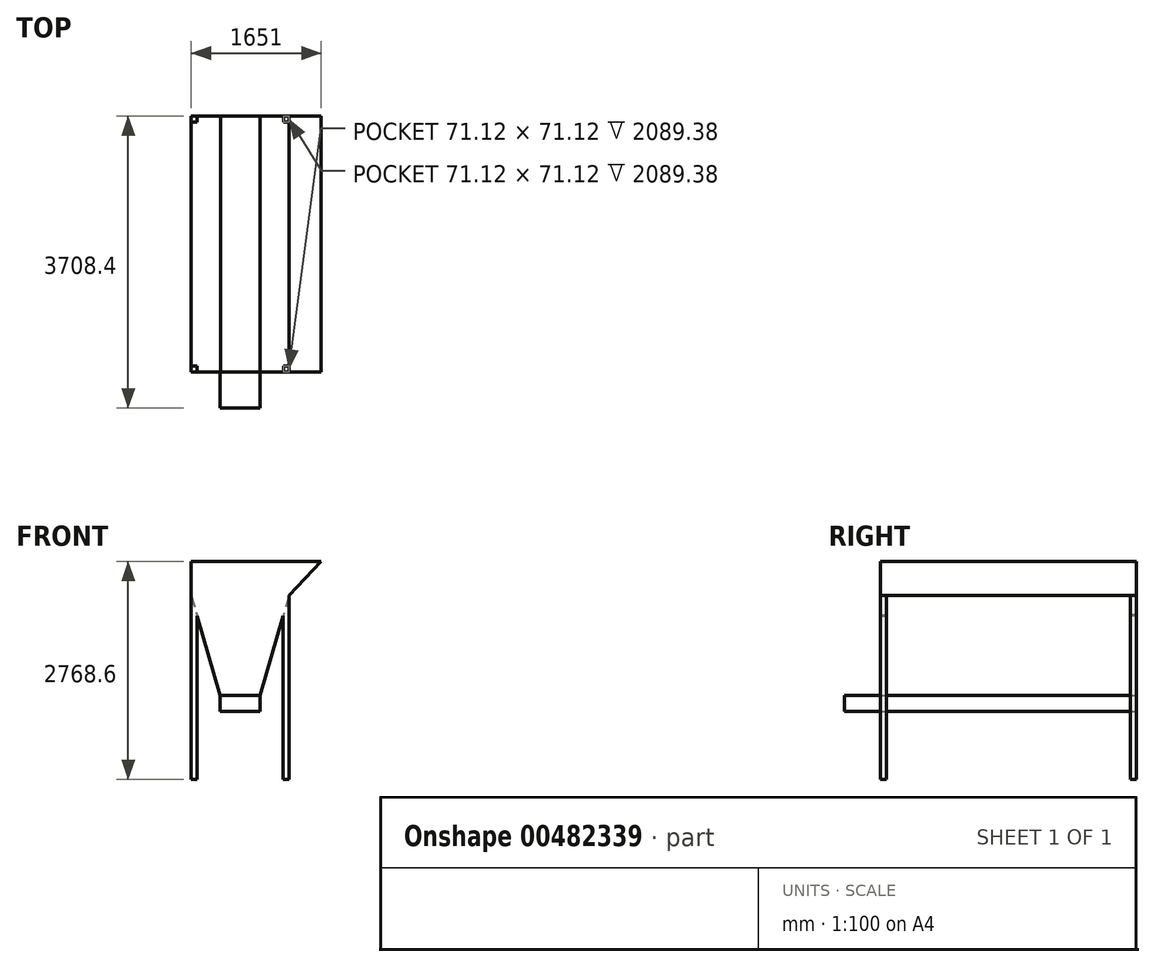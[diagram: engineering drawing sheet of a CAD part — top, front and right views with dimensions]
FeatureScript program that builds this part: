
annotation { "Feature Type Name" : "Feature", "Feature Type Description" : "" }
export const myFeature = defineFeature(function(context is Context, id is Id, definition is map)
    precondition{}
    {
        {
            var Q0;
            Q0=qCreatedBy(makeId("Front.planeOp"),FACE);
            var sketch = newSketch(context, id + "F0", { "sketchPlane" : qUnion([Q0])});
            skLineSegment(sketch, "E0", {"start": v(0, 0) * mm, "end": v(508, 0) * mm});
            skLineSegment(sketch, "E1", {"start": v(508, 0) * mm, "end": v(508, 203.2) * mm});
            skLineSegment(sketch, "E2", {"start": v(508, 203.2) * mm, "end": v(0, 203.2) * mm});
            skLineSegment(sketch, "E3", {"start": v(0, 203.2) * mm, "end": v(0, 0) * mm});
            skLineSegment(sketch, "E4", {"start": v(0, 203.2) * mm, "end": v(-368.3, 1473.2) * mm});
            skLineSegment(sketch, "E5", {"start": v(-368.3, 1473.2) * mm, "end": v(876.3, 1473.2) * mm});
            skLineSegment(sketch, "E6", {"start": v(876.3, 1473.2) * mm, "end": v(508, 203.2) * mm});
            skLineSegment(sketch, "E7", {"start": v(876.3, 1473.2) * mm, "end": v(1282.7, 1905) * mm});
            skLineSegment(sketch, "E8", {"start": v(1282.7, 1905) * mm, "end": v(-368.3, 1905) * mm});
            skLineSegment(sketch, "E9", {"start": v(-368.3, 1905) * mm, "end": v(-368.3, 1473.2) * mm});
            skSolve(sketch);
        }
        {
            var Q0;
            Q0 = qSketchRegion(id + "F0", true);
            extrude(context, id + "F1", {"entities" : qUnion([Q0]), "depth" : 3251.2 * mm, "offsetDistance" : 25.4 * mm});
        }
        {
            var Q0;
            Q0=makeQuery(id+"F1.opExtrude","SWEPT_FACE",FACE,{"disambiguationData":[OSD([sQuery(id+"F0.wireOp",EDGE,"E0")])]});
            cPlane(context, id + "F2", {"entities" : qUnion([Q0]), "cplaneType" : CPlaneType.OFFSET, "offset" : 863.6 * mm, "width" : 152.4 * mm, "height" : 152.4 * mm});
        }
        {
            var Q0;
            Q0=qCreatedBy(id+"F2.planeOp",FACE);
            var sketch = newSketch(context, id + "F3", { "sketchPlane" : qUnion([Q0])});
            skLineSegment(sketch, "E10.bottom", {"start": v(-292.1, 3175) * mm, "end": v(-368.3, 3175) * mm});
            skLineSegment(sketch, "E10.top", {"start": v(-292.1, 3251.2) * mm, "end": v(-368.3, 3251.2) * mm});
            skLineSegment(sketch, "E10.left", {"start": v(-292.1, 3175) * mm, "end": v(-292.1, 3251.2) * mm});
            skLineSegment(sketch, "E10.right", {"start": v(-368.3, 3175) * mm, "end": v(-368.3, 3251.2) * mm});
            skLineSegment(sketch, "E11.bottom", {"start": v(800.1, 3175) * mm, "end": v(876.3, 3175) * mm});
            skLineSegment(sketch, "E11.top", {"start": v(800.1, 3251.2) * mm, "end": v(876.3, 3251.2) * mm});
            skLineSegment(sketch, "E11.left", {"start": v(800.1, 3175) * mm, "end": v(800.1, 3251.2) * mm});
            skLineSegment(sketch, "E11.right", {"start": v(876.3, 3175) * mm, "end": v(876.3, 3251.2) * mm});
            skLineSegment(sketch, "E12.bottom", {"start": v(-292.1, 76.2) * mm, "end": v(-368.3, 76.2) * mm});
            skLineSegment(sketch, "E12.top", {"start": v(-292.1, 0) * mm, "end": v(-368.3, 0) * mm});
            skLineSegment(sketch, "E12.left", {"start": v(-292.1, 76.2) * mm, "end": v(-292.1, 0) * mm});
            skLineSegment(sketch, "E12.right", {"start": v(-368.3, 76.2) * mm, "end": v(-368.3, 0) * mm});
            skLineSegment(sketch, "E13.bottom", {"start": v(800.1, 76.2) * mm, "end": v(876.3, 76.2) * mm});
            skLineSegment(sketch, "E13.top", {"start": v(800.1, 0) * mm, "end": v(876.3, 0) * mm});
            skLineSegment(sketch, "E13.left", {"start": v(800.1, 76.2) * mm, "end": v(800.1, 0) * mm});
            skLineSegment(sketch, "E13.right", {"start": v(876.3, 76.2) * mm, "end": v(876.3, 0) * mm});
            skSolve(sketch);
        }
        {
            var Q0;
            Q0 = qSketchRegion(id + "F3", true);
            extrude(context, id + "F4", {"entities" : qUnion([Q0]), "operationType" : NewBodyOperationType.ADD, "endBound" : BoundingType.UP_TO_NEXT, "oppositeDirection" : true, "depth" : 25.4 * mm, "offsetDistance" : 25.4 * mm});
        }
        {
            var Q0;
            Q0=makeQuery(id+"F4.boolean.opBoolean","MERGE",FACE,{"derivedFrom":[makeQuery(id+"F1.opExtrude","CAP_FACE",FACE,{"disambiguationData":[OSD([sQuery(id+"F0.wireOp",EDGE,"E0"),sQuery(id+"F0.wireOp",EDGE,"E1"),sQuery(id+"F0.wireOp",EDGE,"E3"),sQuery(id+"F0.wireOp",EDGE,"E4"),sQuery(id+"F0.wireOp",EDGE,"E6"),sQuery(id+"F0.wireOp",EDGE,"E7"),sQuery(id+"F0.wireOp",EDGE,"E8"),sQuery(id+"F0.wireOp",EDGE,"E9")])],"isStart":false}),makeQuery(id+"F4.opExtrude","SWEPT_FACE",FACE,{"disambiguationData":[OSD([sQuery(id+"F3.wireOp",EDGE,"E10.top")])]}),makeQuery(id+"F4.opExtrude","SWEPT_FACE",FACE,{"disambiguationData":[OSD([sQuery(id+"F3.wireOp",EDGE,"E11.top")])]})]});
            var sketch = newSketch(context, id + "F5", { "sketchPlane" : qUnion([Q0])});
            skLineSegment(sketch, "E14.bottom", {"start": v(0, 0) * mm, "end": v(508, 0) * mm});
            skLineSegment(sketch, "E14.top", {"start": v(0, 203.2) * mm, "end": v(508, 203.2) * mm});
            skLineSegment(sketch, "E14.left", {"start": v(0, 0) * mm, "end": v(0, 203.2) * mm});
            skLineSegment(sketch, "E14.right", {"start": v(508, 0) * mm, "end": v(508, 203.2) * mm});
            skSolve(sketch);
        }
        {
            var Q0;
            Q0 = qSketchRegion(id + "F5", true);
            extrude(context, id + "F6", {"entities" : qUnion([Q0]), "operationType" : NewBodyOperationType.ADD, "depth" : 457.2 * mm, "offsetDistance" : 25.4 * mm});
        }
        {
            var Q0;
            Q0=makeQuery(id+"F1.opExtrude","SWEPT_FACE",FACE,{"disambiguationData":[OSD([sQuery(id+"F0.wireOp",EDGE,"E8")])]});
            var Q1;
            Q1=makeQuery(id+"F4.boolean.opBoolean","MERGE",FACE,{"derivedFrom":[makeQuery(id+"F1.opExtrude","SWEPT_FACE",FACE,{"disambiguationData":[OSD([sQuery(id+"F0.wireOp",EDGE,"E9")])]}),makeQuery(id+"F4.opExtrude","SWEPT_FACE",FACE,{"disambiguationData":[OSD([sQuery(id+"F3.wireOp",EDGE,"E10.right")])]}),makeQuery(id+"F4.opExtrude","SWEPT_FACE",FACE,{"disambiguationData":[OSD([sQuery(id+"F3.wireOp",EDGE,"E12.right")])]})]});
            shell(context, id + "F7", {"entities" : qUnion([Q0, Q1]), "thickness" : 2.54 * mm});
        }
    });
